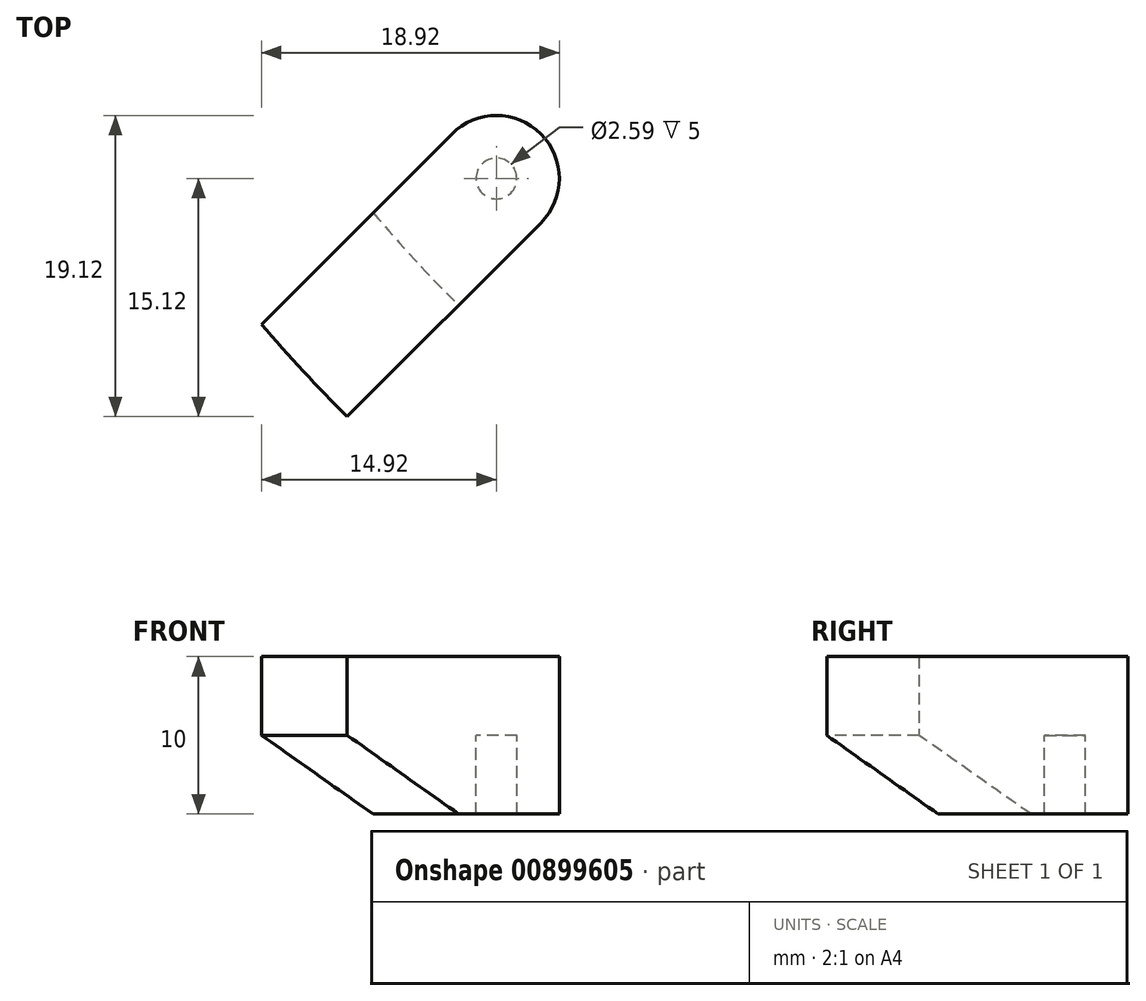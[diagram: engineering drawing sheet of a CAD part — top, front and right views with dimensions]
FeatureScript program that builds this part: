
annotation { "Feature Type Name" : "Feature", "Feature Type Description" : "" }
export const myFeature = defineFeature(function(context is Context, id is Id, definition is map)
    precondition{}
    {
        {
            var Q0;
            Q0=qCreatedBy(makeId("Top.planeOp"),FACE);
            var sketch = newSketch(context, id + "F0", { "sketchPlane" : qUnion([Q0])});
            skPoint(sketch, "E0.middle", {"position": v(0, 0) * mm});
            skCircle(sketch, "E1", {"center": v(0, 0) * mm, "radius": 104.69 * mm});
            skCircle(sketch, "E2", {"center": v(0, 0) * mm, "radius": 98 * mm});
            skPoint(sketch, "E3.middle", {"position": v(59.5, 54.5) * mm});
            skLineSegment(sketch, "E4", {"start": v(62.33, 51.67) * mm, "end": v(74.42, 63.76) * mm});
            skLineSegment(sketch, "E5", {"start": v(56.67, 57.33) * mm, "end": v(68.97, 69.62) * mm});
            skArc(sketch, "E6", {"start": v(56.67, 57.33) * mm, "mid": v(56.67, 51.67) * mm, "end": v(62.33, 51.67) * mm});
            skLineSegment(sketch, "E7.1.0", {"start": v(-62.33, -51.67) * mm, "end": v(-74.42, -63.76) * mm});
            skLineSegment(sketch, "E7.1.1", {"start": v(-56.67, -57.33) * mm, "end": v(-68.97, -69.62) * mm});
            skPoint(sketch, "E7.1.2", {"position": v(-59.5, -54.5) * mm});
            skArc(sketch, "E7.1.3", {"start": v(-56.67, -57.33) * mm, "mid": v(-56.67, -51.67) * mm, "end": v(-62.33, -51.67) * mm});
            skArc(sketch, "E8.1.0", {"start": v(62.05, -51.46) * mm, "mid": v(56.41, -51.95) * mm, "end": v(56.9, -57.59) * mm});
            skLineSegment(sketch, "E8.1.1", {"start": v(62.05, -51.46) * mm, "end": v(75.37, -62.64) * mm});
            skLineSegment(sketch, "E8.1.2", {"start": v(56.9, -57.59) * mm, "end": v(70, -68.58) * mm});
            skLineSegment(sketch, "E8.anchor1", {"start": v(0, 0) * mm, "end": v(59.5, 54.5) * mm, "construction": true});
            skLineSegment(sketch, "E8.anchor2", {"start": v(0, 0) * mm, "end": v(59.48, -54.52) * mm, "construction": true});
            skPoint(sketch, "E9.1.0", {"position": v(-59.48, 54.52) * mm});
            skArc(sketch, "E9.1.1", {"start": v(-62.05, 51.46) * mm, "mid": v(-56.41, 51.95) * mm, "end": v(-56.9, 57.59) * mm});
            skLineSegment(sketch, "E9.1.2", {"start": v(-56.9, 57.59) * mm, "end": v(-70, 68.58) * mm});
            skLineSegment(sketch, "E9.1.3", {"start": v(-62.05, 51.46) * mm, "end": v(-75.37, 62.64) * mm});
            skLineSegment(sketch, "E9.anchor1", {"start": v(0, 0) * mm, "end": v(-59.5, -54.5) * mm, "construction": true});
            skLineSegment(sketch, "E9.anchor2", {"start": v(0, 0) * mm, "end": v(-59.48, 54.52) * mm, "construction": true});
            skSolve(sketch);
        }
        {
            var Q0;
            {var subQ0=sQuery(id+"F0.wireOp",EDGE,"E7.1.0");Q0=makeQuery(id+"F0.imprint","IMPRINT",FACE,{"disambiguationData":[TD([[makeQuery(id+"F0.imprint","IMPRINT",EDGE,{"derivedFrom":subQ0}),1.0]])]});}
            extrude(context, id + "F1", {"entities" : qUnion([Q0]), "depth" : 5 * mm, "offsetDistance" : 25 * mm});
        }
        {
            var Q0;
            {var subQ0=sQuery(id+"F0.wireOp",EDGE,"E7.1.0");Q0=makeQuery(id+"F0.imprint","IMPRINT",FACE,{"disambiguationData":[TD([[makeQuery(id+"F0.imprint","IMPRINT",EDGE,{"derivedFrom":subQ0}),1.0]])]});}
            extrude(context, id + "F2", {"entities" : qUnion([Q0]), "operationType" : NewBodyOperationType.ADD, "oppositeDirection" : true, "depth" : 5 * mm, "offsetDistance" : 25 * mm});
        }
        {
            var Q0;
            Q0=makeQuery(id+"F2.opExtrude","CAP_EDGE",EDGE,{"disambiguationData":[OSD([sQuery(id+"F0.wireOp",EDGE,"E2")])],"isStart":false});
            chamfer(context, id + "F3", {"entities" : qUnion([Q0]), "chamferType" : ChamferType.TWO_OFFSETS, "width1" : 5 * mm, "oppositeDirection" : false, "width2" : 10 * mm, "tangentPropagation" : true});
        }
        {
            var Q0;
            Q0=sQuery(id+"F0.wireOp",VERTEX,"E7.1.2");
            var Q1;
            Q1=makeQuery(id+"F1.opExtrude","SWEPT_BODY",BODY,{"disambiguationData":[OSD([sQuery(id+"F0.wireOp",EDGE,"E2"),sQuery(id+"F0.wireOp",EDGE,"E7.1.0"),sQuery(id+"F0.wireOp",EDGE,"E7.1.1"),sQuery(id+"F0.wireOp",EDGE,"E7.1.3")])]});
            hole(context, id + "F4", {"style" : HoleStyle.SIMPLE, "endStyle" : HoleEndStyle.THROUGH, "standardTappedOrClearance" : lookupTablePath({ "fit" : "Normal (ASME)", "standard" : "ANSI", "size" : "#2", "type" : "Clearance" }), "standardBlindInLast" : lookupTablePath({ "fit" : "Normal", "standard" : "ANSI", "size" : "#2", "type" : "Clearance" }), "holeDiameter" : 2.6 * mm, "majorDiameter" : 2.18 * mm, "isTappedThrough" : true, "tappedDepth" : 12 * mm, "tapClearance" : 3, "locations" : qUnion([Q0]), "scope" : qUnion([Q1])});
        }
    });
